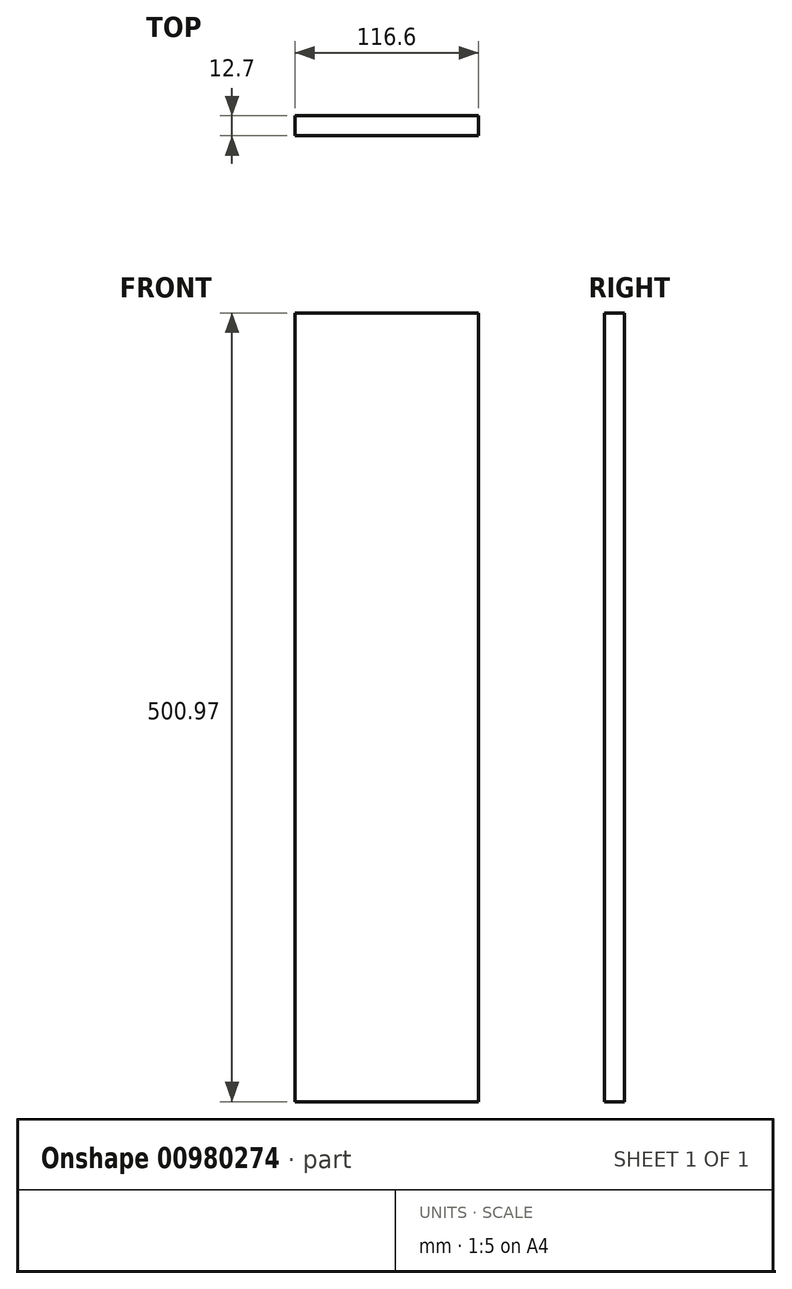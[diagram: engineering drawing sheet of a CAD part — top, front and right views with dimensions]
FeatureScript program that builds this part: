
annotation { "Feature Type Name" : "Feature", "Feature Type Description" : "" }
export const myFeature = defineFeature(function(context is Context, id is Id, definition is map)
    precondition{}
    {
        {
            var Q0;
            Q0=qCreatedBy(makeId("Front.planeOp"),FACE);
            var sketch = newSketch(context, id + "F0", { "sketchPlane" : qUnion([Q0])});
            skLineSegment(sketch, "E0.bottom", {"start": v(216.12, 39.36) * mm, "end": v(99.52, 39.36) * mm});
            skLineSegment(sketch, "E0.top", {"start": v(216.12, -461.61) * mm, "end": v(99.52, -461.61) * mm});
            skLineSegment(sketch, "E0.left", {"start": v(216.12, 39.36) * mm, "end": v(216.12, -461.61) * mm});
            skLineSegment(sketch, "E0.right", {"start": v(99.52, 39.36) * mm, "end": v(99.52, -461.61) * mm});
            skSolve(sketch);
        }
        {
            var Q0;
            Q0=makeQuery(id+"F0.imprint","IMPRINT",FACE,{"disambiguationData":[TD([[makeQuery(id+"F0.imprint","IMPRINT",EDGE,{"derivedFrom":sQuery(id+"F0.wireOp",EDGE,"E0.bottom")}),1.0]])]});
            extrude(context, id + "F1", {"entities" : qUnion([Q0]), "depth" : 12.7 * mm, "offsetDistance" : 25.4 * mm});
        }
    });
